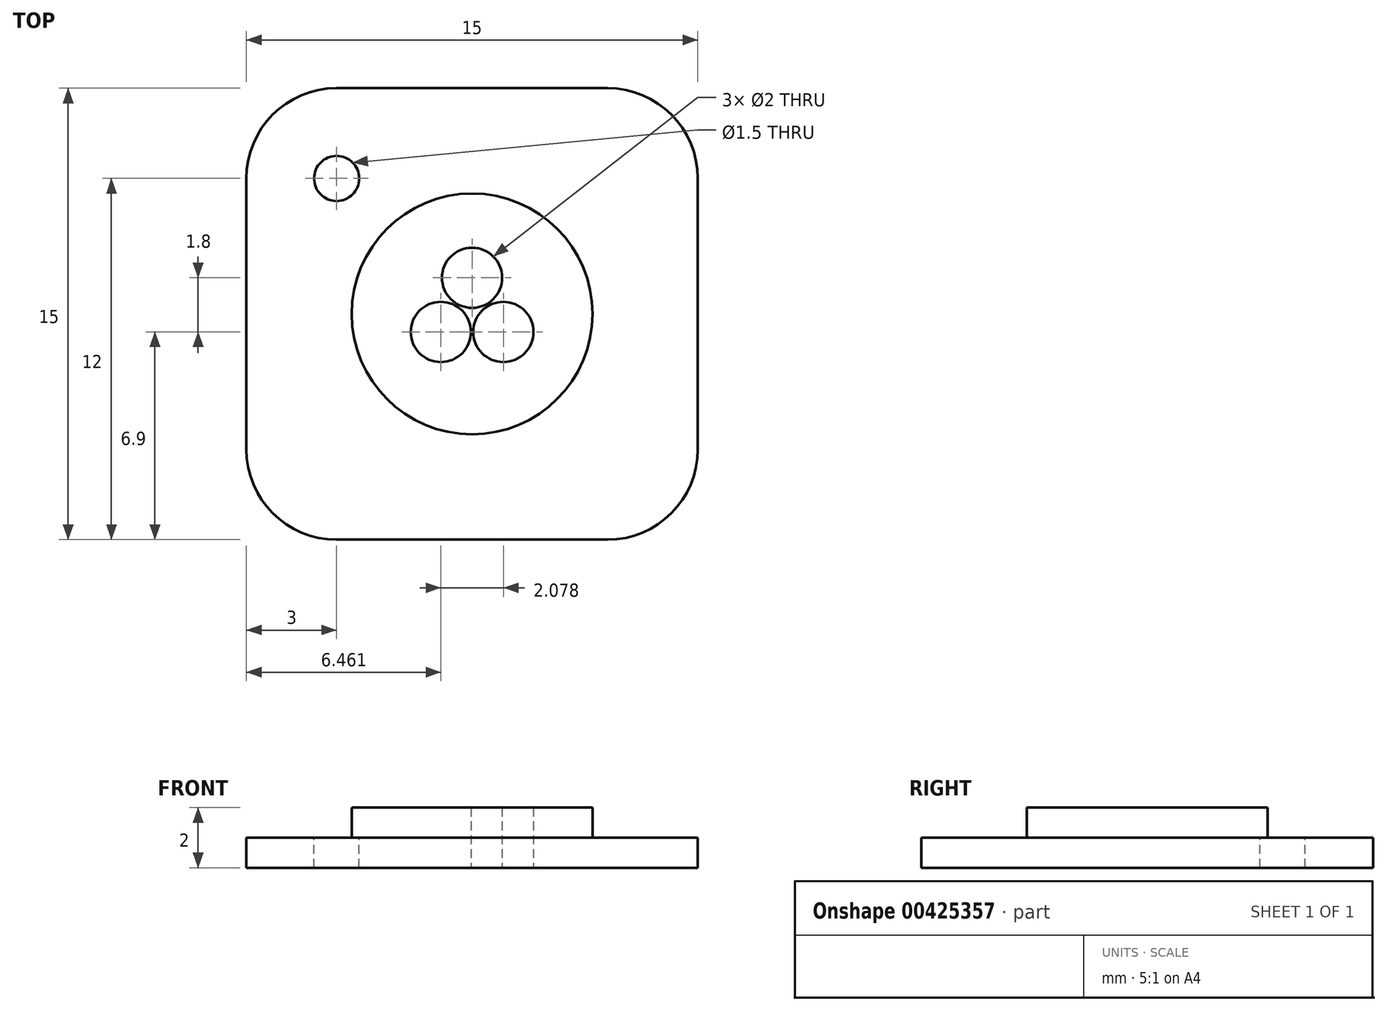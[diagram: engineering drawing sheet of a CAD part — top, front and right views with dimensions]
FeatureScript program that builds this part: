
annotation { "Feature Type Name" : "Feature", "Feature Type Description" : "" }
export const myFeature = defineFeature(function(context is Context, id is Id, definition is map)
    precondition{}
    {
        {
            var Q0;
            Q0=qCreatedBy(makeId("Top.planeOp"),FACE);
            var sketch = newSketch(context, id + "F0", { "sketchPlane" : qUnion([Q0])});
            skCircle(sketch, "E0", {"center": v(0, 0) * mm, "radius": 4 * mm});
            skCircle(sketch, "E1", {"center": v(0, 1.2) * mm, "radius": 1 * mm});
            skLineSegment(sketch, "E2", {"start": v(0, 0) * mm, "end": v(0, 6.05) * mm, "construction": true});
            skCircle(sketch, "E3.1.0", {"center": v(-1.04, -0.6) * mm, "radius": 1 * mm});
            skCircle(sketch, "E3.2.0", {"center": v(1.04, -0.6) * mm, "radius": 1 * mm});
            skSolve(sketch);
        }
        {
            var Q0;
            Q0=makeQuery(id+"F0.imprint","IMPRINT",FACE,{"disambiguationData":[TD([[makeQuery(id+"F0.imprint","IMPRINT",EDGE,{"derivedFrom":sQuery(id+"F0.wireOp",EDGE,"02fqeQfE-6nJA-oOzn-TiH2-VcBi5M3waSDN")}),-1.0]])]});
            var Q1;
            Q1=makeQuery(id+"F0.imprint","IMPRINT",FACE,{"disambiguationData":[TD([[makeQuery(id+"F0.imprint","IMPRINT",EDGE,{"derivedFrom":sQuery(id+"F0.wireOp",EDGE,"E0")}),1.0]])]});
            extrude(context, id + "F1", {"entities" : qUnion([Q0, Q1]), "depth" : 1 * mm});
        }
        {
            var Q0;
            Q0=makeQuery(id+"F1.opExtrude","CAP_FACE",FACE,{"disambiguationData":[OSD([sQuery(id+"F0.wireOp",EDGE,"02fqeQfE-6nJA-oOzn-TiH2-VcBi5M3waSDN"),sQuery(id+"F0.wireOp",EDGE,"E0")])],"isStart":true});
            var sketch = newSketch(context, id + "F2", { "sketchPlane" : qUnion([Q0])});
            skCircle(sketch, "E4", {"center": v(0, 0) * mm, "radius": 1 * mm});
            skCircle(sketch, "E5", {"center": v(0, 0) * mm, "radius": 5 * mm});
            skLineSegment(sketch, "E6.bottom", {"start": v(-7.5, -7.5) * mm, "end": v(7.5, -7.5) * mm});
            skLineSegment(sketch, "E6.top", {"start": v(-7.5, 7.5) * mm, "end": v(7.5, 7.5) * mm});
            skLineSegment(sketch, "E6.left", {"start": v(-7.5, -7.5) * mm, "end": v(-7.5, 7.5) * mm});
            skLineSegment(sketch, "E6.right", {"start": v(7.5, -7.5) * mm, "end": v(7.5, 7.5) * mm});
            skSolve(sketch);
        }
        {
            var Q0;
            Q0=makeQuery(id+"F2.imprint","IMPRINT",FACE,{"disambiguationData":[TD([[makeQuery(id+"F2.imprint","IMPRINT",EDGE,{"derivedFrom":sQuery(id+"F2.wireOp",EDGE,"E5")}),-1.0]])]});
            var Q1;
            Q1=makeQuery(id+"F2.imprint","IMPRINT",FACE,{"disambiguationData":[TD([[makeQuery(id+"F2.imprint","IMPRINT",EDGE,{"derivedFrom":sQuery(id+"F2.wireOp",EDGE,"E5")}),1.0]])]});
            var Q2;
            Q2=makeQuery(id+"F2.imprint","IMPRINT",FACE,{"disambiguationData":[TD([[makeQuery(id+"F2.imprint","IMPRINT",EDGE,{"derivedFrom":sQuery(id+"F2.wireOp",EDGE,"E4")}),1.0]])]});
            var Q3;
            Q3=makeQuery(id+"F2.imprint","IMPRINT",FACE,{"disambiguationData":[TD([[makeQuery(id+"F2.imprint","IMPRINT",EDGE,{"derivedFrom":makeQuery(id+"F1.opExtrude","CAP_EDGE",EDGE,{"disambiguationData":[OSD([sQuery(id+"F0.wireOp",EDGE,"E0")])],"isStart":true})}),-1.0]])]});
            extrude(context, id + "F3", {"entities" : qUnion([Q0, Q1, Q2, Q3]), "operationType" : NewBodyOperationType.ADD, "depth" : 1 * mm});
        }
        {
            var Q0;
            Q0=makeQuery(id+"F3.opExtrude","SWEPT_EDGE",EDGE,{"disambiguationData":[OSD([sQuery(id+"F2.wireOp",EDGE,"E6.bottom"),sQuery(id+"F2.wireOp",EDGE,"E6.left")])]});
            var Q1;
            Q1=makeQuery(id+"F3.opExtrude","SWEPT_EDGE",EDGE,{"disambiguationData":[OSD([sQuery(id+"F2.wireOp",EDGE,"E6.bottom"),sQuery(id+"F2.wireOp",EDGE,"E6.right")])]});
            var Q2;
            Q2=makeQuery(id+"F3.opExtrude","SWEPT_EDGE",EDGE,{"disambiguationData":[OSD([sQuery(id+"F2.wireOp",EDGE,"E6.top"),sQuery(id+"F2.wireOp",EDGE,"E6.left")])]});
            var Q3;
            Q3=makeQuery(id+"F3.opExtrude","SWEPT_EDGE",EDGE,{"disambiguationData":[OSD([sQuery(id+"F2.wireOp",EDGE,"E6.top"),sQuery(id+"F2.wireOp",EDGE,"E6.right")])]});
            fillet(context, id + "F4", {"entities" : qUnion([Q0, Q1, Q2, Q3]), "radius" : 3 * mm, "tangentPropagation" : true, "allowEdgeOverflow" : false});
        }
        {
            var Q0;
            Q0=makeQuery(id+"F3.opExtrude","CAP_FACE",FACE,{"disambiguationData":[OSD([sQuery(id+"F2.wireOp",EDGE,"E4"),sQuery(id+"F2.wireOp",EDGE,"E6.bottom"),sQuery(id+"F2.wireOp",EDGE,"E6.top"),sQuery(id+"F2.wireOp",EDGE,"E6.left"),sQuery(id+"F2.wireOp",EDGE,"E6.right")])],"isStart":true});
            var sketch = newSketch(context, id + "F5", { "sketchPlane" : qUnion([Q0])});
            skCircle(sketch, "E7", {"center": v(-4.5, 4.5) * mm, "radius": 0.75 * mm});
            skSolve(sketch);
        }
        {
            var Q0;
            Q0=qSketchRegion(id+"F5",true);
            extrude(context, id + "F6", {"entities" : qUnion([Q0]), "operationType" : NewBodyOperationType.REMOVE, "oppositeDirection" : true, "depth" : 25 * mm});
        }
    });
